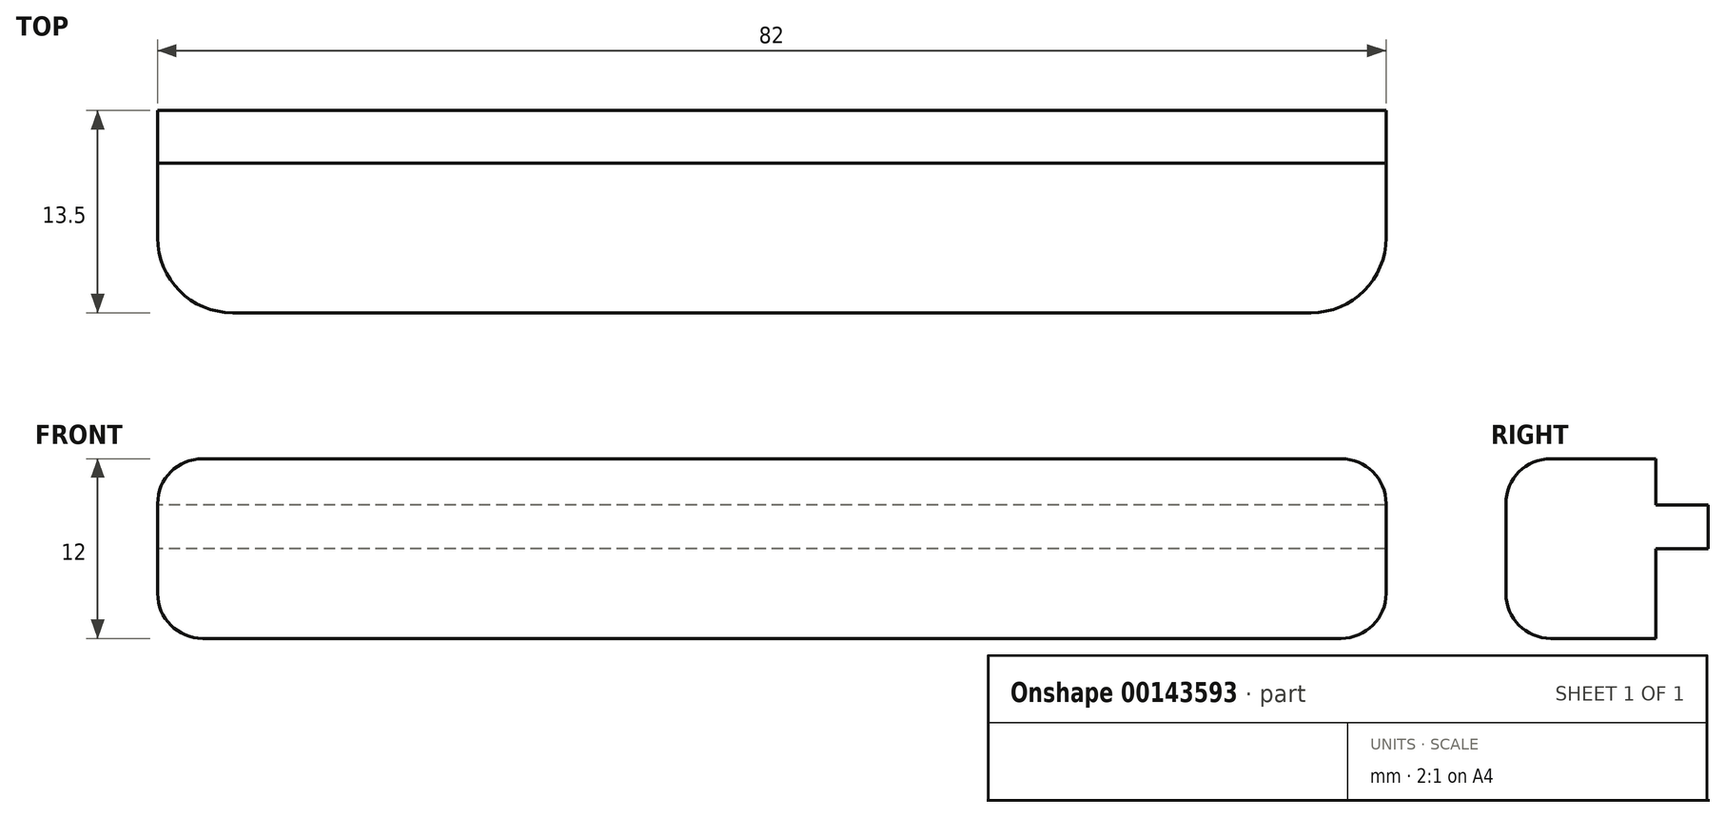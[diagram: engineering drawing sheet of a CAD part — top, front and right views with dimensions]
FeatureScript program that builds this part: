
annotation { "Feature Type Name" : "Feature", "Feature Type Description" : "" }
export const myFeature = defineFeature(function(context is Context, id is Id, definition is map)
    precondition{}
    {
        {
            var Q0;
            Q0=qCreatedBy(makeId("Right.planeOp"),FACE);
            var sketch = newSketch(context, id + "F0", { "sketchPlane" : qUnion([Q0])});
            skLineSegment(sketch, "E0", {"start": v(0, 0) * mm, "end": v(0, 9) * mm});
            skLineSegment(sketch, "E1", {"start": v(0, 0) * mm, "end": v(6.5, 0) * mm});
            skLineSegment(sketch, "E2", {"start": v(0, 9) * mm, "end": v(6.5, 9) * mm});
            skLineSegment(sketch, "E3", {"start": v(6.5, 9) * mm, "end": v(6.5, 5.8) * mm});
            skLineSegment(sketch, "E4", {"start": v(6.5, 5.8) * mm, "end": v(10, 5.8) * mm});
            skLineSegment(sketch, "E5", {"start": v(10, 5.8) * mm, "end": v(10, 3) * mm});
            skLineSegment(sketch, "E6", {"start": v(10, 3) * mm, "end": v(6.5, 3) * mm});
            skLineSegment(sketch, "E7", {"start": v(6.5, 3) * mm, "end": v(6.5, 0) * mm});
            skSolve(sketch);
        }
        {
            var Q0;
            Q0=makeQuery(id+"F0.imprint","IMPRINT",FACE,{"disambiguationData":[TD([[makeQuery(id+"F0.imprint","IMPRINT",EDGE,{"derivedFrom":sQuery(id+"F0.wireOp",EDGE,"E0")}),-1.0]])]});
            extrude(context, id + "F1", {"entities" : qUnion([Q0]), "depth" : 41.5 * mm});
        }
        {
            var Q0;
            Q0=makeQuery(id+"F1.opExtrude","CAP_FACE",FACE,{"disambiguationData":[OSD([sQuery(id+"F0.wireOp",EDGE,"E0"),sQuery(id+"F0.wireOp",EDGE,"E1"),sQuery(id+"F0.wireOp",EDGE,"E2"),sQuery(id+"F0.wireOp",EDGE,"E3"),sQuery(id+"F0.wireOp",EDGE,"E4"),sQuery(id+"F0.wireOp",EDGE,"E5"),sQuery(id+"F0.wireOp",EDGE,"E6"),sQuery(id+"F0.wireOp",EDGE,"E7")])],"isStart":true});
            extrude(context, id + "F2", {"entities" : qUnion([Q0]), "operationType" : NewBodyOperationType.ADD, "depth" : 40.5 * mm});
        }
        {
            var Q0;
            {var subQ0=sQuery(id+"F0.wireOp",EDGE,"E1");Q0=makeQuery(id+"F2.boolean.opBoolean","MERGE",FACE,{"derivedFrom":[makeQuery(id+"F1.opExtrude","SWEPT_FACE",FACE,{"disambiguationData":[OSD([subQ0])]}),makeQuery(id+"F2.opExtrude","SWEPT_FACE",FACE,{"disambiguationData":[OSD([subQ0])]})]});}
            extrude(context, id + "F3", {"entities" : qUnion([Q0]), "operationType" : NewBodyOperationType.ADD, "depth" : 3 * mm});
        }
        {
            var Q0;
            {var subQ0=sQuery(id+"F0.wireOp",EDGE,"E4");Q0=makeQuery(id+"F2.boolean.opBoolean","MERGE",FACE,{"derivedFrom":[makeQuery(id+"F1.opExtrude","SWEPT_FACE",FACE,{"disambiguationData":[OSD([subQ0])]}),makeQuery(id+"F2.opExtrude","SWEPT_FACE",FACE,{"disambiguationData":[OSD([subQ0])]})]});}
            extrude(context, id + "F4", {"entities" : qUnion([Q0]), "operationType" : NewBodyOperationType.ADD, "depth" : 0.1 * mm});
        }
        {
            var Q0;
            {var subQ0=sQuery(id+"F0.wireOp",EDGE,"E0");Q0=makeQuery(id+"F3.boolean.opBoolean","MERGE",FACE,{"derivedFrom":[makeQuery(id+"F2.boolean.opBoolean","MERGE",FACE,{"derivedFrom":[makeQuery(id+"F1.opExtrude","SWEPT_FACE",FACE,{"disambiguationData":[OSD([subQ0])]}),makeQuery(id+"F2.opExtrude","SWEPT_FACE",FACE,{"disambiguationData":[OSD([subQ0])]})]}),makeQuery(id+"F3.opExtrude","SWEPT_FACE",FACE,{"disambiguationData":[OSD([subQ0,sQuery(id+"F0.wireOp",EDGE,"E1")])]})]});}
            extrude(context, id + "F5", {"entities" : qUnion([Q0]), "operationType" : NewBodyOperationType.ADD, "depth" : 3.5 * mm});
        }
        {
            var Q0;
            {var subQ0=sQuery(id+"F0.wireOp",EDGE,"E1");var subQ1=sQuery(id+"F0.wireOp",EDGE,"E0");Q0=makeQuery(id+"F5.opExtrude","CAP_EDGE",EDGE,{"disambiguationData":[OSD([subQ1,subQ0]),TDD([makeQuery(id+"F3.boolean.opBoolean","MERGE",EDGE,{"derivedFrom":[makeQuery(id+"F1.opExtrude","CAP_EDGE",EDGE,{"disambiguationData":[OSD([subQ1])],"isStart":false}),makeQuery(id+"F3.opExtrude","SWEPT_EDGE",EDGE,{"disambiguationData":[OSD([subQ1,subQ0]),TDD([makeQuery(id+"F1.opExtrude","CAP_VERTEX",VERTEX,{"disambiguationData":[OSD([subQ1,subQ0])],"isStart":false})])]})]})])],"isStart":false});}
            var Q1;
            {var subQ0=sQuery(id+"F0.wireOp",EDGE,"E1");var subQ1=sQuery(id+"F0.wireOp",EDGE,"E0");Q1=makeQuery(id+"F5.opExtrude","CAP_EDGE",EDGE,{"disambiguationData":[OSD([subQ1,subQ0]),TDD([makeQuery(id+"F3.boolean.opBoolean","MERGE",EDGE,{"derivedFrom":[makeQuery(id+"F2.opExtrude","CAP_EDGE",EDGE,{"disambiguationData":[OSD([subQ1])],"isStart":false}),makeQuery(id+"F3.opExtrude","SWEPT_EDGE",EDGE,{"disambiguationData":[OSD([subQ1,subQ0]),TDD([makeQuery(id+"F2.opExtrude","CAP_VERTEX",VERTEX,{"disambiguationData":[OSD([subQ1,subQ0])],"isStart":false})])]})]})])],"isStart":false});}
            fillet(context, id + "F6", {"entities" : qUnion([Q0, Q1]), "radius" : 5 * mm, "tangentPropagation" : true, "allowEdgeOverflow" : false});
        }
        {
            var Q0;
            Q0=makeQuery(id+"F5.opExtrude","CAP_EDGE",EDGE,{"disambiguationData":[OSD([sQuery(id+"F0.wireOp",EDGE,"E0"),sQuery(id+"F0.wireOp",EDGE,"E2")])],"isStart":false});
            var Q1;
            {var subQ0=sQuery(id+"F0.wireOp",EDGE,"E1");var subQ1=sQuery(id+"F0.wireOp",EDGE,"E0");Q1=makeQuery(id+"F5.opExtrude","CAP_EDGE",EDGE,{"disambiguationData":[OSD([subQ1,subQ0]),TDD([makeQuery(id+"F3.opExtrude","CAP_EDGE",EDGE,{"disambiguationData":[OSD([subQ1,subQ0])],"isStart":false})])],"isStart":false});}
            fillet(context, id + "F7", {"entities" : qUnion([Q0, Q1]), "radius" : 3 * mm, "tangentPropagation" : true, "allowEdgeOverflow" : false});
        }
    });
